# Revit family: QF_OSCARTEK_LA_CROSSE_G1650_cat
name_source: partatom
category: Specialty Equipment
units: mm (PartAtom-declared; Revit-internal decimal feet)

## family parameters
Always vertical = Yes
Cut with Voids When Loaded = No
Enable Cutting in Views = No
Maintain Annotation Orientation = No
Part Type = Normal
Room Calculation Point = No
Round Connector Dimension = Use Diameter
Shared = No
Work Plane-Based = No

## types (1)
- QF_OSCARTEK_LA_CROSSE_G1650_cat
    Apparent Power = 0 VA
    BTUH = 3966.0 Btu/h
    Conn Conduit = Yes
    Cycle = 60 Hz
    Default Elevation = 0"
    Depth = 45 3/8"
    Description = GELATO SHOWCASE
    Elec Conn Connection Height = 0"
    Elec Conn RI Height = 0"
    FL Amps = 9 A
    Foodservice Equipment Identifier = Yes
    Height = 45 1/4"
    Identify Quantity as Lot = Yes
    Indirect Waste Connection Height = 0"
    Indirect Waste Flow = 0 GPM
    Indirect Waste Size = 0"
    Length = 67 5/16"
    Manufacturer = OSCARTEK
    Max Overcurrent Protection = 0 A
    Min Ckt Ampacity = 0 A
    Model = LA CROSSE PG1650
    Number of Poles = 1
    Phase = 1
    Refrigerant Type = R404A
    Refrigerant Volume = 0.00 kip
    Volts = 208 V
    Waste Water Discharge Temperature = -460 °F
    Watts = 3400 W
    Weight in Pounds = 639

## geometry (parser evidence)
native form markers: Blend x10, Sweep x5
no freeform markers — native parametric forms only
